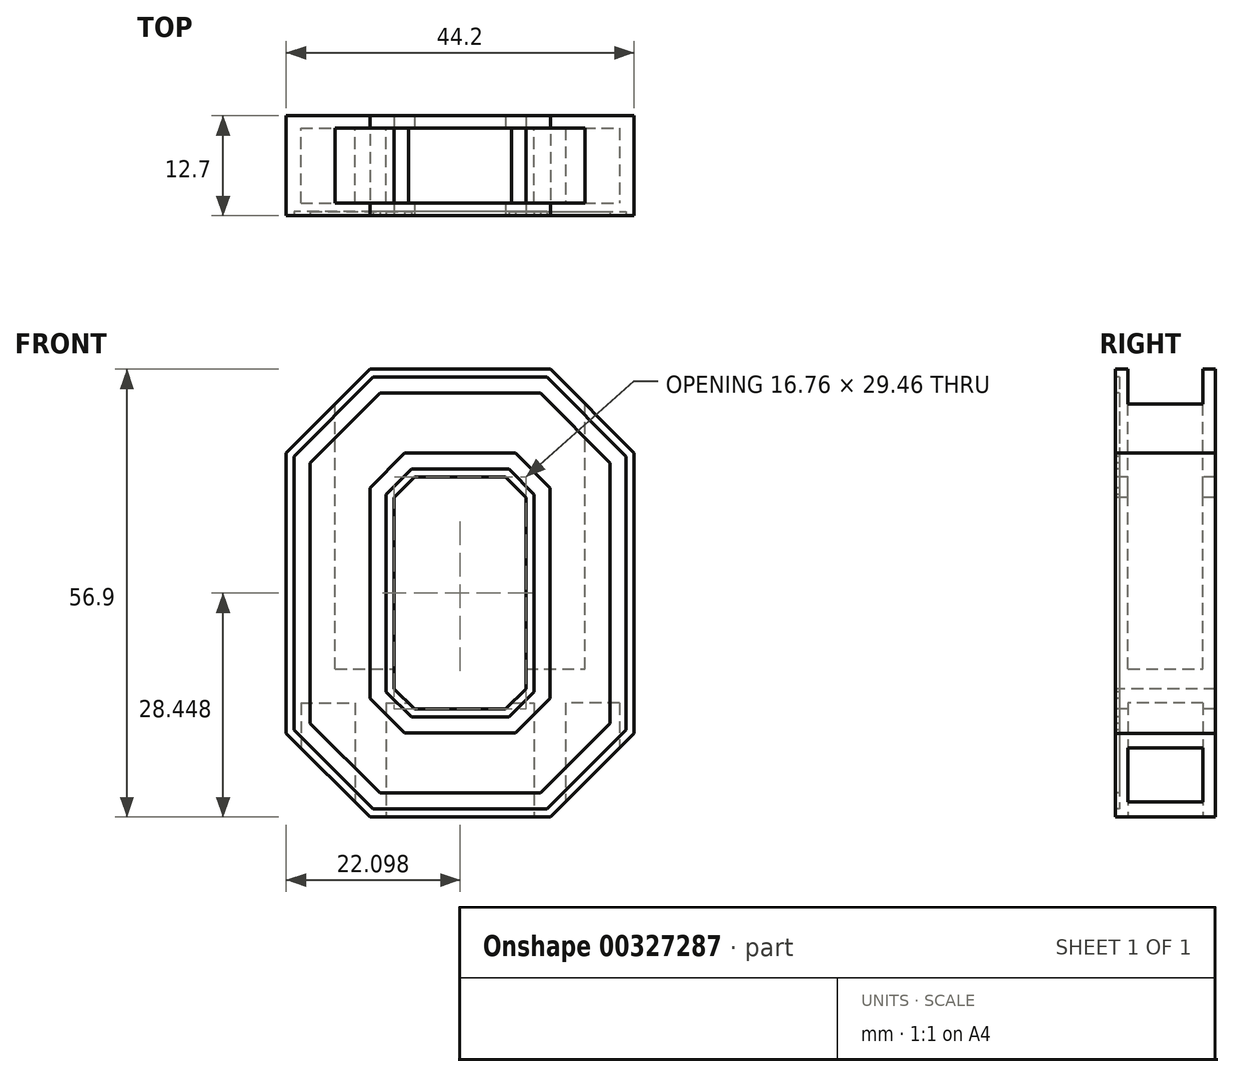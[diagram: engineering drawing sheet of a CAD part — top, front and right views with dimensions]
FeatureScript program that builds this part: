
annotation { "Feature Type Name" : "Feature", "Feature Type Description" : "" }
export const myFeature = defineFeature(function(context is Context, id is Id, definition is map)
    precondition{}
    {
        {
            var Q0;
            Q0=qCreatedBy(makeId("Front.planeOp"),FACE);
            var sketch = newSketch(context, id + "F0", { "sketchPlane" : qUnion([Q0])});
            skLineSegment(sketch, "E0", {"start": v(86.78, 59.94) * mm, "end": v(72.7, 59.94) * mm});
            skLineSegment(sketch, "E1", {"start": v(72.7, 59.94) * mm, "end": v(68.3, 55.55) * mm});
            skLineSegment(sketch, "E2", {"start": v(68.3, 55.55) * mm, "end": v(68.3, 28.77) * mm});
            skLineSegment(sketch, "E3", {"start": v(68.3, 28.77) * mm, "end": v(72.7, 24.38) * mm});
            skLineSegment(sketch, "E4", {"start": v(72.7, 24.38) * mm, "end": v(86.78, 24.38) * mm});
            skPoint(sketch, "E5", {"position": v(68.3, 42.16) * mm});
            skLineSegment(sketch, "E6", {"start": v(79.74, 59.94) * mm, "end": v(79.74, 24.38) * mm});
            skLineSegment(sketch, "E7.MirrorCS", {"start": v(91.17, 28.77) * mm, "end": v(86.78, 24.38) * mm});
            skLineSegment(sketch, "E8.MirrorCS", {"start": v(86.78, 59.94) * mm, "end": v(91.17, 55.55) * mm});
            skLineSegment(sketch, "E9.MirrorCS", {"start": v(91.17, 55.55) * mm, "end": v(91.17, 28.77) * mm});
            skLineSegment(sketch, "E10.0", {"start": v(89.94, 67.56) * mm, "end": v(98.79, 58.7) * mm});
            skLineSegment(sketch, "E10.1", {"start": v(98.79, 58.7) * mm, "end": v(98.79, 25.6) * mm});
            skLineSegment(sketch, "E10.2", {"start": v(89.94, 67.56) * mm, "end": v(69.54, 67.56) * mm});
            skLineSegment(sketch, "E10.3", {"start": v(98.79, 25.6) * mm, "end": v(89.94, 16.76) * mm});
            skLineSegment(sketch, "E10.4", {"start": v(69.54, 67.56) * mm, "end": v(60.69, 58.7) * mm});
            skLineSegment(sketch, "E10.5", {"start": v(60.69, 58.7) * mm, "end": v(60.69, 25.6) * mm});
            skLineSegment(sketch, "E10.6", {"start": v(60.69, 25.6) * mm, "end": v(69.54, 16.76) * mm});
            skLineSegment(sketch, "E10.7", {"start": v(69.54, 16.76) * mm, "end": v(89.94, 16.76) * mm});
            skLineSegment(sketch, "E11.0", {"start": v(90.78, 69.59) * mm, "end": v(100.82, 59.55) * mm});
            skLineSegment(sketch, "E11.1", {"start": v(100.82, 59.55) * mm, "end": v(100.82, 24.77) * mm});
            skLineSegment(sketch, "E11.2", {"start": v(90.78, 69.59) * mm, "end": v(68.7, 69.59) * mm});
            skLineSegment(sketch, "E11.3", {"start": v(100.82, 24.77) * mm, "end": v(90.78, 14.73) * mm});
            skLineSegment(sketch, "E11.4", {"start": v(68.7, 69.59) * mm, "end": v(58.66, 59.55) * mm});
            skLineSegment(sketch, "E11.5", {"start": v(58.66, 59.55) * mm, "end": v(58.66, 24.77) * mm});
            skLineSegment(sketch, "E11.6", {"start": v(58.66, 24.77) * mm, "end": v(68.7, 14.73) * mm});
            skLineSegment(sketch, "E11.7", {"start": v(68.7, 14.73) * mm, "end": v(90.78, 14.73) * mm});
            skLineSegment(sketch, "E12.0", {"start": v(91.2, 70.6) * mm, "end": v(101.84, 59.97) * mm});
            skLineSegment(sketch, "E12.1", {"start": v(101.84, 59.97) * mm, "end": v(101.84, 24.35) * mm});
            skLineSegment(sketch, "E12.2", {"start": v(91.2, 70.6) * mm, "end": v(68.28, 70.6) * mm});
            skLineSegment(sketch, "E12.3", {"start": v(101.84, 24.35) * mm, "end": v(91.2, 13.7) * mm});
            skLineSegment(sketch, "E12.4", {"start": v(68.28, 70.6) * mm, "end": v(57.64, 59.97) * mm});
            skLineSegment(sketch, "E12.5", {"start": v(57.64, 59.97) * mm, "end": v(57.64, 24.35) * mm});
            skLineSegment(sketch, "E12.6", {"start": v(57.64, 24.35) * mm, "end": v(68.28, 13.7) * mm});
            skLineSegment(sketch, "E12.7", {"start": v(68.28, 13.7) * mm, "end": v(91.2, 13.7) * mm});
            skLineSegment(sketch, "E13.0", {"start": v(85.94, 57.9) * mm, "end": v(89.14, 54.7) * mm});
            skLineSegment(sketch, "E13.1", {"start": v(89.14, 54.7) * mm, "end": v(89.14, 29.6) * mm});
            skLineSegment(sketch, "E13.2", {"start": v(85.94, 57.9) * mm, "end": v(73.54, 57.9) * mm});
            skLineSegment(sketch, "E13.3", {"start": v(89.14, 29.6) * mm, "end": v(85.94, 26.4) * mm});
            skLineSegment(sketch, "E13.4", {"start": v(73.54, 57.9) * mm, "end": v(70.34, 54.7) * mm});
            skLineSegment(sketch, "E13.5", {"start": v(70.34, 54.7) * mm, "end": v(70.34, 29.6) * mm});
            skLineSegment(sketch, "E13.6", {"start": v(70.34, 29.6) * mm, "end": v(73.54, 26.4) * mm});
            skLineSegment(sketch, "E13.7", {"start": v(73.54, 26.4) * mm, "end": v(85.94, 26.4) * mm});
            skLineSegment(sketch, "E14.0", {"start": v(85.52, 56.89) * mm, "end": v(88.12, 54.29) * mm});
            skLineSegment(sketch, "E14.1", {"start": v(88.12, 54.29) * mm, "end": v(88.12, 30.03) * mm});
            skLineSegment(sketch, "E14.2", {"start": v(85.52, 56.89) * mm, "end": v(73.96, 56.89) * mm});
            skLineSegment(sketch, "E14.3", {"start": v(88.12, 30.03) * mm, "end": v(85.52, 27.43) * mm});
            skLineSegment(sketch, "E14.4", {"start": v(73.96, 56.89) * mm, "end": v(71.36, 54.29) * mm});
            skLineSegment(sketch, "E14.5", {"start": v(71.36, 54.29) * mm, "end": v(71.36, 30.03) * mm});
            skLineSegment(sketch, "E14.6", {"start": v(71.36, 30.03) * mm, "end": v(73.96, 27.43) * mm});
            skLineSegment(sketch, "E14.7", {"start": v(73.96, 27.43) * mm, "end": v(85.52, 27.43) * mm});
            skSolve(sketch);
        }
        {
            var Q0;
            Q0 = qSketchRegion(id + "F0", true);
            var Q1;
            Q1=makeQuery(id+"F0.imprint","IMPRINT",FACE,{"disambiguationData":[TD([[makeQuery(id+"F0.imprint","IMPRINT",EDGE,{"derivedFrom":sQuery(id+"F0.wireOp",EDGE,"E10.0")}),1.0]])]});
            var Q2;
            {var subQ8=sQuery(id+"F0.wireOp",EDGE,"E1");Q2=makeQuery(id+"F0.imprint","IMPRINT",FACE,{"disambiguationData":[TD([[makeQuery(id+"F0.imprint","IMPRINT",EDGE,{"derivedFrom":subQ8}),-1.0]])]});}
            var Q3;
            {var subQ11=sQuery(id+"F0.wireOp",EDGE,"E1");Q3=makeQuery(id+"F0.imprint","IMPRINT",FACE,{"disambiguationData":[TD([[makeQuery(id+"F0.imprint","IMPRINT",EDGE,{"derivedFrom":subQ11}),1.0]])]});}
            var Q4;
            {var subQ12=sQuery(id+"F0.wireOp",EDGE,"E13.4");Q4=makeQuery(id+"F0.imprint","IMPRINT",FACE,{"disambiguationData":[TD([[makeQuery(id+"F0.imprint","IMPRINT",EDGE,{"derivedFrom":subQ12}),1.0]])]});}
            var Q5;
            {var subQ6=sQuery(id+"F0.wireOp",EDGE,"E13.0");Q5=makeQuery(id+"F0.imprint","IMPRINT",FACE,{"disambiguationData":[TD([[makeQuery(id+"F0.imprint","IMPRINT",EDGE,{"derivedFrom":subQ6}),-1.0]])]});}
            var Q6;
            {var subQ5=sQuery(id+"F0.wireOp",EDGE,"E7.MirrorCS");Q6=makeQuery(id+"F0.imprint","IMPRINT",FACE,{"disambiguationData":[TD([[makeQuery(id+"F0.imprint","IMPRINT",EDGE,{"derivedFrom":subQ5}),-1.0]])]});}
            extrude(context, id + "F1", {"entities" : qUnion([Q0, Q1, Q2, Q3, Q4, Q5, Q6]), "oppositeDirection" : true, "depth" : 12.7 * mm});
        }
        {
            var Q0;
            Q0=makeQuery(id+"F0.imprint","IMPRINT",FACE,{"disambiguationData":[TD([[makeQuery(id+"F0.imprint","IMPRINT",EDGE,{"derivedFrom":sQuery(id+"F0.wireOp",EDGE,"E10.0")}),1.0]])]});
            var Q1;
            {var subQ11=sQuery(id+"F0.wireOp",EDGE,"E1");Q1=makeQuery(id+"F0.imprint","IMPRINT",FACE,{"disambiguationData":[TD([[makeQuery(id+"F0.imprint","IMPRINT",EDGE,{"derivedFrom":subQ11}),1.0]])]});}
            var Q2;
            {var subQ5=sQuery(id+"F0.wireOp",EDGE,"E7.MirrorCS");Q2=makeQuery(id+"F0.imprint","IMPRINT",FACE,{"disambiguationData":[TD([[makeQuery(id+"F0.imprint","IMPRINT",EDGE,{"derivedFrom":subQ5}),-1.0]])]});}
            extrude(context, id + "F2", {"entities" : qUnion([Q0, Q1, Q2]), "operationType" : NewBodyOperationType.REMOVE, "oppositeDirection" : true, "depth" : 0.5 * mm});
        }
        {
            var Q0;
            Q0=makeQuery(id+"F1.opExtrude","SWEPT_FACE",FACE,{"disambiguationData":[OSD([sQuery(id+"F0.wireOp",EDGE,"E12.2")])]});
            var sketch = newSketch(context, id + "F3", { "sketchPlane" : qUnion([Q0])});
            skLineSegment(sketch, "E15.bottom", {"start": v(63.86, 11.11) * mm, "end": v(95.61, 11.11) * mm});
            skLineSegment(sketch, "E15.top", {"start": v(63.86, 1.59) * mm, "end": v(95.61, 1.59) * mm});
            skLineSegment(sketch, "E15.left", {"start": v(63.86, 11.11) * mm, "end": v(63.86, 1.59) * mm});
            skLineSegment(sketch, "E15.right", {"start": v(95.61, 11.11) * mm, "end": v(95.61, 1.59) * mm});
            skLineSegment(sketch, "E16", {"start": v(79.74, 0) * mm, "end": v(79.74, 12.7) * mm});
            skLineSegment(sketch, "E17", {"start": v(79.74, 6.35) * mm, "end": v(51.28, 6.35) * mm});
            skPoint(sketch, "E17.endSnap0", {"position": v(68.28, 6.35) * mm});
            skSolve(sketch);
        }
        {
            var Q0;
            Q0 = qSketchRegion(id + "F3", true);
            extrude(context, id + "F4", {"entities" : qUnion([Q0]), "operationType" : NewBodyOperationType.REMOVE, "oppositeDirection" : true, "depth" : 38.1 * mm});
        }
        {
            var Q0;
            Q0=makeQuery(id+"F1.opExtrude","SWEPT_FACE",FACE,{"disambiguationData":[OSD([sQuery(id+"F0.wireOp",EDGE,"E12.7")])]});
            var sketch = newSketch(context, id + "F5", { "sketchPlane" : qUnion([Q0])});
            skLineSegment(sketch, "E18.bottom", {"start": v(70.35, -1.59) * mm, "end": v(89.13, -1.59) * mm});
            skLineSegment(sketch, "E18.top", {"start": v(70.35, -11.11) * mm, "end": v(89.13, -11.11) * mm});
            skLineSegment(sketch, "E18.left", {"start": v(70.35, -1.59) * mm, "end": v(70.35, -11.11) * mm});
            skLineSegment(sketch, "E18.right", {"start": v(89.13, -1.59) * mm, "end": v(89.13, -11.11) * mm});
            skLineSegment(sketch, "E19", {"start": v(79.74, 0) * mm, "end": v(79.74, -12.7) * mm});
            skLineSegment(sketch, "E20", {"start": v(91.2, -6.35) * mm, "end": v(68.28, -6.35) * mm});
            skLineSegment(sketch, "E21.bottom", {"start": v(59.51, -1.59) * mm, "end": v(66.37, -1.59) * mm});
            skLineSegment(sketch, "E21.top", {"start": v(59.51, -11.11) * mm, "end": v(66.37, -11.11) * mm});
            skLineSegment(sketch, "E21.left", {"start": v(59.51, -1.59) * mm, "end": v(59.51, -11.11) * mm});
            skLineSegment(sketch, "E21.right", {"start": v(66.37, -1.59) * mm, "end": v(66.37, -11.11) * mm});
            skLineSegment(sketch, "E22.MirrorCS", {"start": v(99.96, -1.59) * mm, "end": v(93.1, -1.59) * mm});
            skLineSegment(sketch, "E23.MirrorCS", {"start": v(99.96, -11.11) * mm, "end": v(93.1, -11.11) * mm});
            skLineSegment(sketch, "E24.MirrorCS", {"start": v(93.1, -1.59) * mm, "end": v(93.1, -11.11) * mm});
            skLineSegment(sketch, "E25.MirrorCS", {"start": v(99.96, -1.59) * mm, "end": v(99.96, -11.11) * mm});
            skSolve(sketch);
        }
        {
            var Q0;
            Q0 = qSketchRegion(id + "F5", true);
            extrude(context, id + "F6", {"entities" : qUnion([Q0]), "operationType" : NewBodyOperationType.REMOVE, "oppositeDirection" : true, "depth" : 14.48 * mm});
        }
    });
